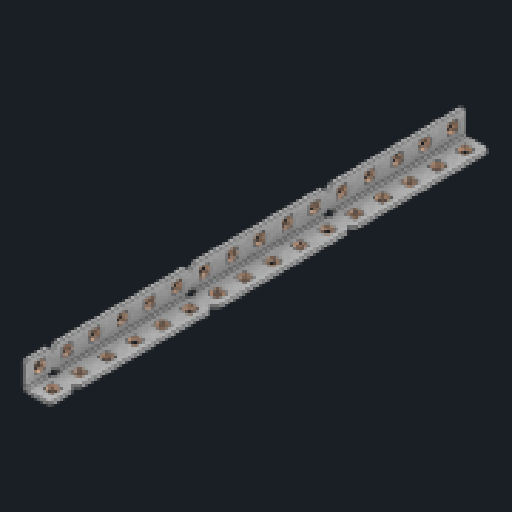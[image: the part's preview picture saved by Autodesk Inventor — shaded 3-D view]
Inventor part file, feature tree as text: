
AUTODESK INVENTOR PART (.ipt)
format: ipt  version: 2025 (Build 290162000, 162)  size: 758,272 bytes
history: native  units: in
note: dims shown in document units (in); Inventor stores cm internally (conversion verified against a paired STEP export)
features: other x73, sketch x2, sheet_metal_op x1
ambient origin geometry x8: Origin, YZ Plane, XZ Plane, XY Plane, X Axis, Y Axis, Z Axis, Center Point
bodies: Solid1 (feature_tree)
feature tree (76):
  other  "Alu Angle 1x1x16.ipt"
  other  "Solid1::Alu Angle 1x1x16.ipt"
  other  "TaggingFeature1"
  sketch  "Sketch1"  dims[d0=0.3937in]
  sketch  "Sketch2"  dims[d1=0.0625in]
  sheet_metal_op  "Body Pattern Sketch"
  other  "Arc Length"
  other  "Diagonal Plane"
  other  "Srf1"
  other  "Srf2"
  other  "Srf3"
  other  "Srf4"
  other  "Srf5"
  other  "Srf6"
  other  "Srf7"
  other  "Srf8"
  other  "Srf9"
  other  "Srf10"
  other  "Srf11"
  other  "Srf12"
  other  "Srf13"
  other  "Srf14"
  other  "Srf15"
  other  "Srf16"
  other  "Srf17"
  other  "Srf18"
  other  "Srf19"
  other  "Srf20"
  other  "Srf21"
  other  "Srf22"
  other  "Srf23"
  other  "Srf24"
  other  "Srf25"
  other  "Srf26"
  other  "Srf27"
  other  "Srf28"
  other  "Srf29"
  other  "Srf30"
  other  "Srf31"
  other  "Srf32"
  other  "Srf33"
  other  "Srf34"
  other  "Srf91::Derived"
  other  "Srf92::Derived"
  other  "Srf856::Derived"
  other  "Srf857::Derived"
  other  "Srf858::Derived"
  other  "Srf859::Derived"
  other  "Srf860::Derived"
  other  "Srf861::Derived"
  other  "Srf1383::Derived"
  other  "Srf1384::Derived"
  other  "Srf1385::Derived"
  other  "Srf1386::Derived"
  other  "Srf1387::Derived"
  other  "Srf1388::Derived"
  other  "Srf1389::Derived"
  other  "Srf1390::Derived"
  other  "Srf1391::Derived"
  other  "Srf1275::Derived"
  other  "Srf1276::Derived"
  other  "Srf1278::Derived"
  other  "Srf1279::Derived"
  other  "Srf1280::Derived"
  other  "Srf1281::Derived"
  other  "Srf1282::Derived"
  other  "Srf1283::Derived"
  other  "Srf1475::Derived"
  other  "Srf1476::Derived"
  other  "Srf1477::Derived"
  other  "Srf1478::Derived"
  other  "Srf1479::Derived"
  other  "Srf1480::Derived"
  other  "Srf1481::Derived"
  other  "Srf1482::Derived"
  other  "Srf1483::Derived"
